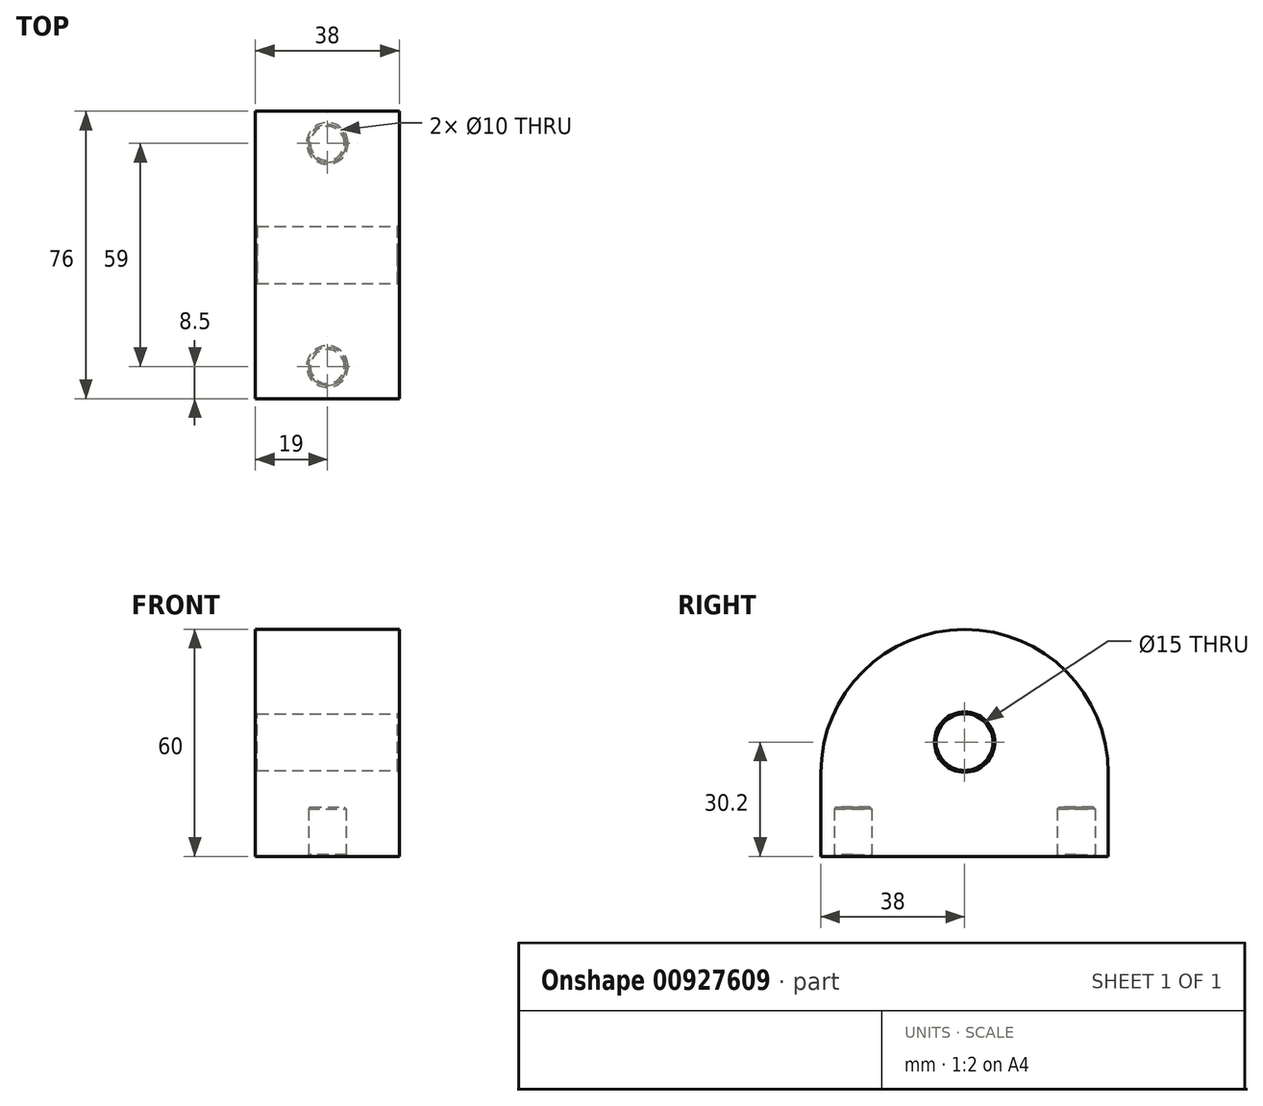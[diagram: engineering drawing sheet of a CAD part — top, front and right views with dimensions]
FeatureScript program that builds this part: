
annotation { "Feature Type Name" : "Feature", "Feature Type Description" : "" }
export const myFeature = defineFeature(function(context is Context, id is Id, definition is map)
    precondition{}
    {
        {
            var Q0;
            Q0=qCreatedBy(makeId("Right.planeOp"),FACE);
            var sketch = newSketch(context, id + "F0", { "sketchPlane" : qUnion([Q0])});
            skLineSegment(sketch, "E0", {"start": v(0, 41.62) * mm, "end": v(0, -38.09) * mm, "construction": true});
            skLineSegment(sketch, "E1", {"start": v(0, 0) * mm, "end": v(38, 0) * mm});
            skLineSegment(sketch, "E2", {"start": v(38, 0) * mm, "end": v(38, 22) * mm});
            skLineSegment(sketch, "E3", {"start": v(0, 60) * mm, "end": v(0, 60) * mm});
            skLineSegment(sketch, "E4.MirrorCS", {"start": v(-38, 0) * mm, "end": v(-38, 22) * mm});
            skLineSegment(sketch, "E5.MirrorCS", {"start": v(0, 0) * mm, "end": v(-38, 0) * mm});
            skArc(sketch, "E6.filletArc", {"start": v(0, 60) * mm, "mid": v(-26.87, 48.87) * mm, "end": v(-38, 22) * mm});
            skPoint(sketch, "E7.visualSharp", {"position": v(38, 60) * mm});
            skArc(sketch, "E7.filletArc", {"start": v(38, 22) * mm, "mid": v(26.87, 48.87) * mm, "end": v(0, 60) * mm});
            skLineSegment(sketch, "E8", {"start": v(38, 0) * mm, "end": v(38, 0) * mm});
            skPoint(sketch, "E9.MirrorCS.end.orphan", {"position": v(-38, 0) * mm});
            skPoint(sketch, "E10.orphan", {"position": v(-63.5, 0) * mm});
            skSolve(sketch);
        }
        {
            var Q0;
            Q0=makeQuery(id+"F0.imprint","IMPRINT",FACE,{"disambiguationData":[TD([[makeQuery(id+"F0.imprint","IMPRINT",EDGE,{"derivedFrom":sQuery(id+"F0.wireOp",EDGE,"E1")}),1.0]])]});
            extrude(context, id + "F1", {"entities" : qUnion([Q0]), "oppositeDirection" : true, "depth" : 38 * mm, "offsetDistance" : 25 * mm});
        }
        {
            var Q0;
            Q0=makeQuery(id+"F1.opExtrude","CAP_FACE",FACE,{"disambiguationData":[OSD([sQuery(id+"F0.wireOp",EDGE,"E1"),sQuery(id+"F0.wireOp",EDGE,"RtqcIcoO-Zqee-EfPe-kn9l-3DGsCo8VodxW"),sQuery(id+"F0.wireOp",EDGE,"nnB3ec7W-d7rR-AGD1-NLoB-wS66SehvqZ3F"),sQuery(id+"F0.wireOp",EDGE,"E2"),sQuery(id+"F0.wireOp",EDGE,"E3"),sQuery(id+"F0.wireOp",EDGE,"E3"),sQuery(id+"F0.wireOp",EDGE,"E4.MirrorCS"),sQuery(id+"F0.wireOp",EDGE,"E9.MirrorCS"),sQuery(id+"F0.wireOp",EDGE,"bd062287-7c66-4265-8a4f-764fc5263b430.MirrorCS"),sQuery(id+"F0.wireOp",EDGE,"E5.MirrorCS")])],"isStart":true});
            var sketch = newSketch(context, id + "F2", { "sketchPlane" : qUnion([Q0])});
            skLineSegment(sketch, "E11", {"start": v(0, 41.84) * mm, "end": v(0, -18.68) * mm, "construction": true});
            skCircle(sketch, "E12", {"center": v(0, 30.2) * mm, "radius": 7.5 * mm});
            skPoint(sketch, "E13.startSnap0", {"position": v(-38, 11) * mm});
            skSolve(sketch);
        }
        {
            var Q0;
            Q0 = qSketchRegion(id + "F2", true);
            extrude(context, id + "F3", {"entities" : qUnion([Q0]), "operationType" : NewBodyOperationType.REMOVE, "endBound" : BoundingType.THROUGH_ALL, "oppositeDirection" : true, "depth" : 25 * mm, "offsetDistance" : 25 * mm});
        }
        {
            var Q0;
            Q0=makeQuery(id+"F3.boolean.opBoolean","COPY",FACE,{"derivedFrom":makeQuery(id+"F3.opExtrude","SWEPT_FACE",FACE,{"disambiguationData":[OSD([sQuery(id+"F2.wireOp",EDGE,"E12")])]})});
            var Q1;
            Q1=makeQuery(id+"F3.boolean.opBoolean","COPY",FACE,{"derivedFrom":makeQuery(id+"F3.opExtrude","SWEPT_FACE",FACE,{"disambiguationData":[OSD([sQuery(id+"F2.wireOp",EDGE,"KprJPrfb-A1SH-hbkv-kHAY-yfdFDmoMtXw7")])]})});
            var Q2;
            Q2=makeQuery(id+"F3.boolean.opBoolean","COPY",FACE,{"derivedFrom":makeQuery(id+"F3.opExtrude","SWEPT_FACE",FACE,{"disambiguationData":[OSD([sQuery(id+"F2.wireOp",EDGE,"75147bd4-c1b4-40a2-899b-7924272daf630.MirrorC")])]})});
            chamfer(context, id + "F4", {"entities" : qUnion([Q0, Q1, Q2]), "width" : 0.5 * mm, "tangentPropagation" : true});
        }
        {
            var Q0;
            Q0=makeQuery(id+"F1.opExtrude","SWEPT_FACE",FACE,{"disambiguationData":[OSD([sQuery(id+"F0.wireOp",EDGE,"E1"),sQuery(id+"F0.wireOp",EDGE,"E5.MirrorCS")])]});
            var sketch = newSketch(context, id + "F5", { "sketchPlane" : qUnion([Q0])});
            skLineSegment(sketch, "E14", {"start": v(-19, 89.46) * mm, "end": v(-19, -51.47) * mm, "construction": true});
            skLineSegment(sketch, "E15", {"start": v(-57.1, 29.5) * mm, "end": v(34.93, 29.5) * mm, "construction": true});
            skLineSegment(sketch, "E16", {"start": v(-58.49, -29.5) * mm, "end": v(36.53, -29.5) * mm, "construction": true});
            skCircle(sketch, "E17", {"center": v(-19, -29.5) * mm, "radius": 5 * mm});
            skCircle(sketch, "E18", {"center": v(-19, 29.5) * mm, "radius": 5 * mm});
            skLineSegment(sketch, "E19", {"start": v(-60.26, 0) * mm, "end": v(22.3, 0) * mm, "construction": true});
            skSolve(sketch);
        }
        {
            var Q0;
            Q0=makeQuery(id+"F5.imprint","IMPRINT",FACE,{"disambiguationData":[TD([[makeQuery(id+"F5.imprint","IMPRINT",EDGE,{"derivedFrom":sQuery(id+"F5.wireOp",EDGE,"E18")}),1.0]])]});
            var Q1;
            Q1=makeQuery(id+"F5.imprint","IMPRINT",FACE,{"disambiguationData":[TD([[makeQuery(id+"F5.imprint","IMPRINT",EDGE,{"derivedFrom":sQuery(id+"F5.wireOp",EDGE,"E17")}),1.0]])]});
            extrude(context, id + "F6", {"entities" : qUnion([Q0, Q1]), "operationType" : NewBodyOperationType.REMOVE, "oppositeDirection" : true, "depth" : 13 * mm, "offsetDistance" : 25 * mm});
        }
        {
            var Q0;
            Q0=makeQuery(id+"F6.boolean.opBoolean","COPY",FACE,{"derivedFrom":makeQuery(id+"F6.opExtrude","SWEPT_FACE",FACE,{"disambiguationData":[OSD([sQuery(id+"F5.wireOp",EDGE,"E18")])]})});
            var Q1;
            Q1=makeQuery(id+"F6.boolean.opBoolean","COPY",FACE,{"derivedFrom":makeQuery(id+"F6.opExtrude","SWEPT_FACE",FACE,{"disambiguationData":[OSD([sQuery(id+"F5.wireOp",EDGE,"E17")])]})});
            chamfer(context, id + "F7", {"entities" : qUnion([Q0, Q1]), "width" : 0.5 * mm, "tangentPropagation" : true});
        }
    });
